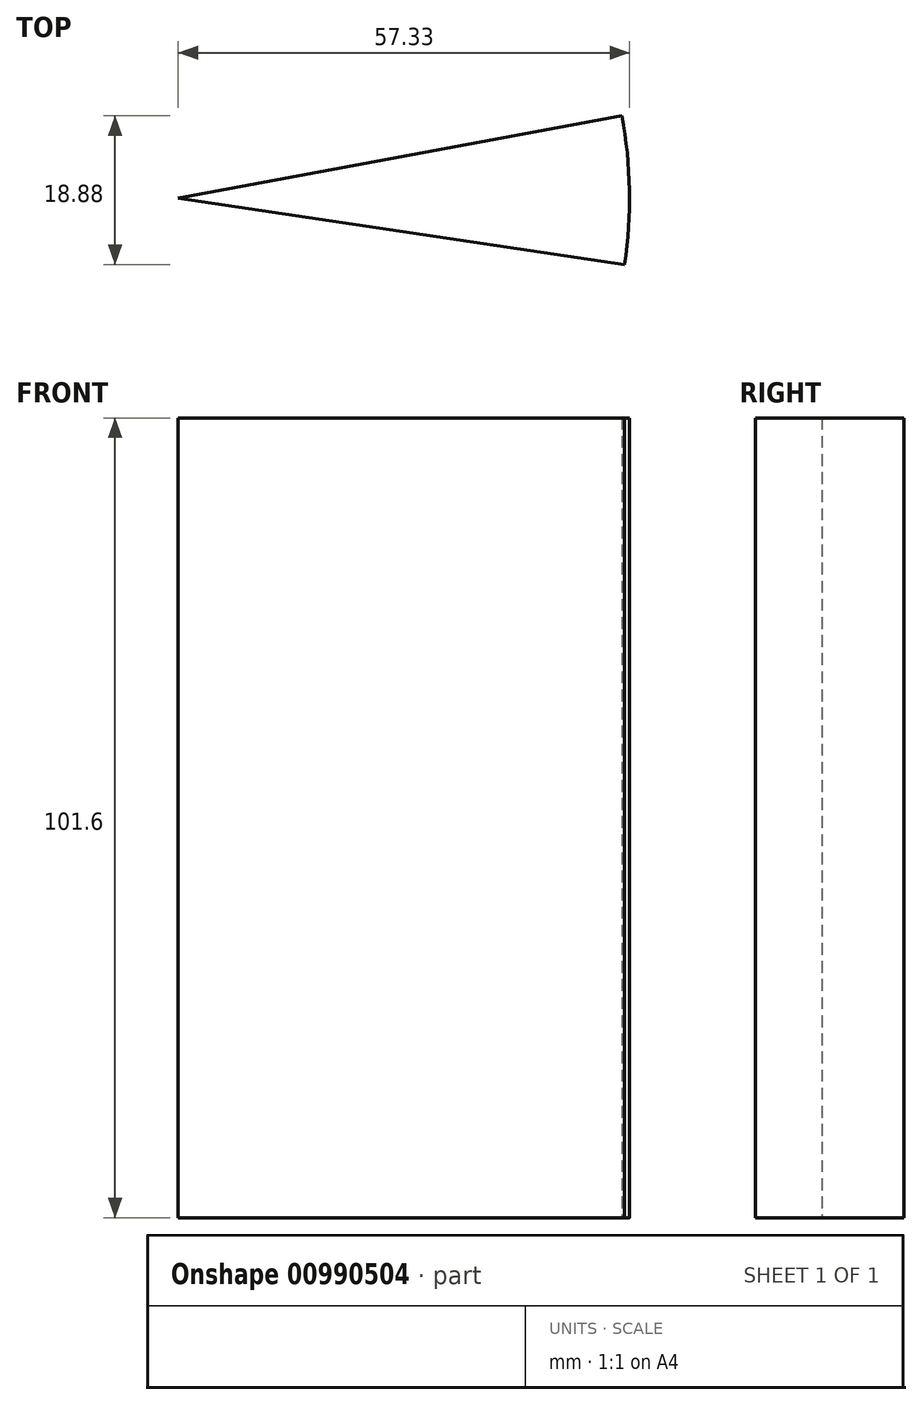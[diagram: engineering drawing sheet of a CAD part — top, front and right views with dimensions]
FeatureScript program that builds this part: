
annotation { "Feature Type Name" : "Feature", "Feature Type Description" : "" }
export const myFeature = defineFeature(function(context is Context, id is Id, definition is map)
    precondition{}
    {
        {
            var Q0;
            Q0=qCreatedBy(makeId("Top.planeOp"),FACE);
            var sketch = newSketch(context, id + "F0", { "sketchPlane" : qUnion([Q0])});
            skLineSegment(sketch, "E0", {"start": v(0, 0) * mm, "end": v(56.7, -8.44) * mm});
            skArc(sketch, "E1", {"start": v(56.7, -8.44) * mm, "mid": v(57.33, 1.01) * mm, "end": v(56.38, 10.44) * mm});
            skLineSegment(sketch, "E2", {"start": v(0, 0) * mm, "end": v(56.38, 10.44) * mm});
            skSolve(sketch);
        }
        {
            var Q0;
            Q0 = qSketchRegion(id + "F0", true);
            extrude(context, id + "F1", {"entities" : qUnion([Q0]), "depth" : 101.6 * mm, "offsetDistance" : 25.4 * mm});
        }
    });
